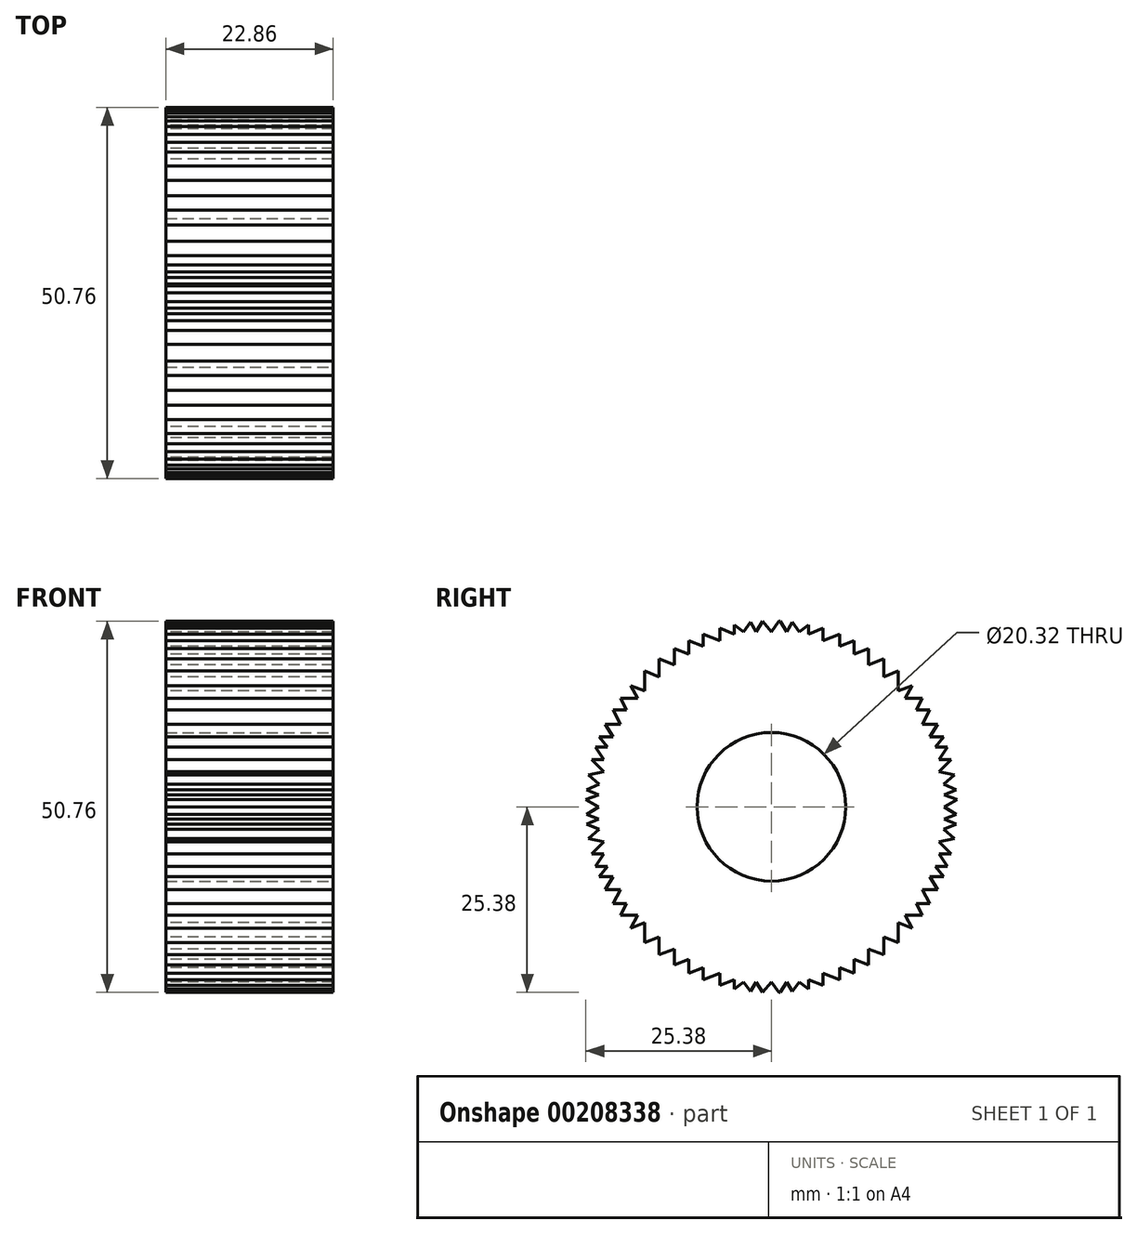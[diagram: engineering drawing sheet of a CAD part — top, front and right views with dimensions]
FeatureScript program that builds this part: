
annotation { "Feature Type Name" : "Feature", "Feature Type Description" : "" }
export const myFeature = defineFeature(function(context is Context, id is Id, definition is map)
    precondition{}
    {
        {
            var Q0;
            Q0=qCreatedBy(makeId("Right.planeOp"),FACE);
            var sketch = newSketch(context, id + "F0", { "sketchPlane" : qUnion([Q0])});
            skCircle(sketch, "E0", {"center": v(0, 0) * mm, "radius": 25.4 * mm});
            skLineSegment(sketch, "E1", {"start": v(-19.24, 16.59) * mm, "end": v(-17.33, 15.84) * mm});
            skLineSegment(sketch, "E2", {"start": v(-17.33, 15.84) * mm, "end": v(-17.33, 18.57) * mm});
            skLineSegment(sketch, "E3", {"start": v(-17.33, 18.57) * mm, "end": v(-15.36, 17.8) * mm});
            skLineSegment(sketch, "E4", {"start": v(-15.36, 17.8) * mm, "end": v(-15.36, 20.23) * mm});
            skLineSegment(sketch, "E5", {"start": v(-15.36, 20.23) * mm, "end": v(-13.3, 19.42) * mm});
            skLineSegment(sketch, "E6", {"start": v(-13.3, 19.42) * mm, "end": v(-13.3, 21.64) * mm});
            skLineSegment(sketch, "E7", {"start": v(-13.3, 21.64) * mm, "end": v(-11.3, 20.86) * mm});
            skLineSegment(sketch, "E8", {"start": v(-11.3, 20.86) * mm, "end": v(-11.3, 22.75) * mm});
            skLineSegment(sketch, "E9", {"start": v(-11.3, 22.75) * mm, "end": v(-9.31, 21.96) * mm});
            skLineSegment(sketch, "E10", {"start": v(-9.31, 21.96) * mm, "end": v(-9.31, 23.63) * mm});
            skLineSegment(sketch, "E11", {"start": v(-9.31, 23.63) * mm, "end": v(-7.06, 22.75) * mm});
            skLineSegment(sketch, "E12", {"start": v(-7.06, 22.75) * mm, "end": v(-7.06, 24.4) * mm});
            skLineSegment(sketch, "E13", {"start": v(-7.06, 24.4) * mm, "end": v(-5.1, 23.63) * mm});
            skLineSegment(sketch, "E14", {"start": v(-5.1, 23.63) * mm, "end": v(-5.1, 24.88) * mm});
            skLineSegment(sketch, "E15", {"start": v(-5.1, 24.88) * mm, "end": v(-3.8, 23.93) * mm});
            skLineSegment(sketch, "E16", {"start": v(-3.8, 23.93) * mm, "end": v(-2.85, 25.24) * mm});
            skLineSegment(sketch, "E17", {"start": v(-2.85, 25.24) * mm, "end": v(-2.1, 23.93) * mm});
            skLineSegment(sketch, "E18", {"start": v(-2.1, 23.93) * mm, "end": v(-1.21, 25.37) * mm});
            skLineSegment(sketch, "E19", {"start": v(-1.21, 25.37) * mm, "end": v(0, 23.93) * mm});
            skLineSegment(sketch, "E20", {"start": v(0, 23.93) * mm, "end": v(1, 25.38) * mm});
            skLineSegment(sketch, "E21", {"start": v(-19.24, 16.59) * mm, "end": v(-18.29, 14.84) * mm});
            skPoint(sketch, "E21.endSnap0", {"position": v(-18.29, 16.21) * mm});
            skLineSegment(sketch, "E22", {"start": v(-18.29, 14.84) * mm, "end": v(-20.62, 14.84) * mm});
            skLineSegment(sketch, "E23", {"start": v(-20.62, 14.84) * mm, "end": v(-19.8, 13.24) * mm});
            skLineSegment(sketch, "E24", {"start": v(-19.8, 13.24) * mm, "end": v(-21.68, 13.24) * mm});
            skLineSegment(sketch, "E25", {"start": v(-21.68, 13.24) * mm, "end": v(-20.62, 11.3) * mm});
            skLineSegment(sketch, "E26", {"start": v(-20.62, 11.3) * mm, "end": v(-22.74, 11.3) * mm});
            skLineSegment(sketch, "E27", {"start": v(-22.74, 11.3) * mm, "end": v(-21.68, 9.54) * mm});
            skLineSegment(sketch, "E28", {"start": v(-21.68, 9.54) * mm, "end": v(-23.54, 9.54) * mm});
            skLineSegment(sketch, "E29", {"start": v(-23.54, 9.54) * mm, "end": v(-22.44, 8.17) * mm});
            skLineSegment(sketch, "E30", {"start": v(-22.44, 8.17) * mm, "end": v(-24.05, 8.17) * mm});
            skLineSegment(sketch, "E31", {"start": v(-24.05, 8.17) * mm, "end": v(-22.93, 6.46) * mm});
            skLineSegment(sketch, "E32", {"start": v(-22.93, 6.46) * mm, "end": v(-24.57, 6.46) * mm});
            skLineSegment(sketch, "E33", {"start": v(-24.57, 6.46) * mm, "end": v(-22.93, 4.8) * mm});
            skLineSegment(sketch, "E34", {"start": v(-22.93, 4.8) * mm, "end": v(-25.03, 4.34) * mm});
            skLineSegment(sketch, "E35", {"start": v(-25.03, 4.34) * mm, "end": v(-23.54, 3.1) * mm});
            skLineSegment(sketch, "E36", {"start": v(-23.54, 3.1) * mm, "end": v(-25.3, 2.36) * mm});
            skLineSegment(sketch, "E37", {"start": v(-25.3, 2.36) * mm, "end": v(-23.65, 1.66) * mm});
            skLineSegment(sketch, "E38", {"start": v(-23.65, 1.66) * mm, "end": v(-25.38, 1.01) * mm});
            skLineSegment(sketch, "E39", {"start": v(-25.38, 1.01) * mm, "end": v(-23.65, 0) * mm});
            skLineSegment(sketch, "E40", {"start": v(-23.65, 0) * mm, "end": v(-25.38, -1.1) * mm});
            skLineSegment(sketch, "E41.MirrorCS", {"start": v(2.1, 23.93) * mm, "end": v(1.21, 25.37) * mm});
            skLineSegment(sketch, "E42.MirrorCS", {"start": v(2.85, 25.24) * mm, "end": v(2.1, 23.93) * mm});
            skLineSegment(sketch, "E43.MirrorCS", {"start": v(3.8, 23.93) * mm, "end": v(2.85, 25.24) * mm});
            skLineSegment(sketch, "E44.MirrorCS", {"start": v(5.1, 24.88) * mm, "end": v(3.8, 23.93) * mm});
            skLineSegment(sketch, "E45.MirrorCS", {"start": v(5.1, 23.63) * mm, "end": v(5.1, 24.88) * mm});
            skLineSegment(sketch, "E46.MirrorCS", {"start": v(7.06, 24.4) * mm, "end": v(5.1, 23.63) * mm});
            skLineSegment(sketch, "E47.MirrorCS", {"start": v(7.06, 22.75) * mm, "end": v(7.06, 24.4) * mm});
            skLineSegment(sketch, "E48.MirrorCS", {"start": v(9.31, 23.63) * mm, "end": v(7.06, 22.75) * mm});
            skLineSegment(sketch, "E49.MirrorCS", {"start": v(9.31, 21.96) * mm, "end": v(9.31, 23.63) * mm});
            skLineSegment(sketch, "E50.MirrorCS", {"start": v(11.3, 22.75) * mm, "end": v(9.31, 21.96) * mm});
            skLineSegment(sketch, "E51.MirrorCS", {"start": v(11.3, 20.86) * mm, "end": v(11.3, 22.75) * mm});
            skLineSegment(sketch, "E52.MirrorCS", {"start": v(13.3, 21.64) * mm, "end": v(11.3, 20.86) * mm});
            skLineSegment(sketch, "E53.MirrorCS", {"start": v(13.3, 19.42) * mm, "end": v(13.3, 21.64) * mm});
            skLineSegment(sketch, "E54.MirrorCS", {"start": v(15.36, 20.23) * mm, "end": v(13.3, 19.42) * mm});
            skLineSegment(sketch, "E55.MirrorCS", {"start": v(15.36, 17.8) * mm, "end": v(15.36, 20.23) * mm});
            skLineSegment(sketch, "E56.MirrorCS", {"start": v(17.33, 18.57) * mm, "end": v(15.36, 17.8) * mm});
            skLineSegment(sketch, "E57.MirrorCS", {"start": v(17.33, 15.84) * mm, "end": v(17.33, 18.57) * mm});
            skLineSegment(sketch, "E58.MirrorCS", {"start": v(19.24, 16.59) * mm, "end": v(17.33, 15.84) * mm});
            skLineSegment(sketch, "E59.MirrorCS", {"start": v(19.24, 16.59) * mm, "end": v(18.29, 14.84) * mm});
            skLineSegment(sketch, "E60.MirrorCS", {"start": v(18.29, 14.84) * mm, "end": v(20.62, 14.84) * mm});
            skLineSegment(sketch, "E61.MirrorCS", {"start": v(20.62, 14.84) * mm, "end": v(19.8, 13.24) * mm});
            skLineSegment(sketch, "E62.MirrorCS", {"start": v(19.8, 13.24) * mm, "end": v(21.68, 13.24) * mm});
            skLineSegment(sketch, "E63.MirrorCS", {"start": v(21.68, 13.24) * mm, "end": v(20.62, 11.3) * mm});
            skLineSegment(sketch, "E64.MirrorCS", {"start": v(20.62, 11.3) * mm, "end": v(22.74, 11.3) * mm});
            skLineSegment(sketch, "E65.MirrorCS", {"start": v(22.74, 11.3) * mm, "end": v(21.68, 9.54) * mm});
            skLineSegment(sketch, "E66.MirrorCS", {"start": v(21.68, 9.54) * mm, "end": v(23.54, 9.54) * mm});
            skLineSegment(sketch, "E67.MirrorCS", {"start": v(23.54, 9.54) * mm, "end": v(22.44, 8.17) * mm});
            skLineSegment(sketch, "E68.MirrorCS", {"start": v(22.44, 8.17) * mm, "end": v(24.05, 8.17) * mm});
            skLineSegment(sketch, "E69.MirrorCS", {"start": v(24.05, 8.17) * mm, "end": v(22.93, 6.46) * mm});
            skLineSegment(sketch, "E70.MirrorCS", {"start": v(22.93, 6.46) * mm, "end": v(24.57, 6.46) * mm});
            skLineSegment(sketch, "E71.MirrorCS", {"start": v(24.57, 6.46) * mm, "end": v(22.93, 4.8) * mm});
            skLineSegment(sketch, "E72.MirrorCS", {"start": v(22.93, 4.8) * mm, "end": v(25.03, 4.34) * mm});
            skLineSegment(sketch, "E73.MirrorCS", {"start": v(25.03, 4.34) * mm, "end": v(23.54, 3.1) * mm});
            skLineSegment(sketch, "E74.MirrorCS", {"start": v(23.54, 3.1) * mm, "end": v(25.3, 2.36) * mm});
            skLineSegment(sketch, "E75.MirrorCS", {"start": v(25.3, 2.36) * mm, "end": v(23.65, 1.66) * mm});
            skLineSegment(sketch, "E76.MirrorCS", {"start": v(23.65, 1.66) * mm, "end": v(25.38, 1.01) * mm});
            skLineSegment(sketch, "E77.MirrorCS", {"start": v(25.38, 1.01) * mm, "end": v(23.65, 0) * mm});
            skLineSegment(sketch, "E78.MirrorCS", {"start": v(23.65, 0) * mm, "end": v(25.38, -1.1) * mm});
            skLineSegment(sketch, "E79.MirrorCS", {"start": v(23.65, -1.66) * mm, "end": v(25.38, -1.01) * mm});
            skLineSegment(sketch, "E80.MirrorCS", {"start": v(25.3, -2.36) * mm, "end": v(23.65, -1.66) * mm});
            skLineSegment(sketch, "E81.MirrorCS", {"start": v(23.54, -3.1) * mm, "end": v(25.3, -2.36) * mm});
            skLineSegment(sketch, "E82.MirrorCS", {"start": v(25.03, -4.34) * mm, "end": v(23.54, -3.1) * mm});
            skLineSegment(sketch, "E83.MirrorCS", {"start": v(22.93, -4.8) * mm, "end": v(25.03, -4.34) * mm});
            skLineSegment(sketch, "E84.MirrorCS", {"start": v(24.57, -6.46) * mm, "end": v(22.93, -4.8) * mm});
            skLineSegment(sketch, "E85.MirrorCS", {"start": v(22.93, -6.46) * mm, "end": v(24.57, -6.46) * mm});
            skLineSegment(sketch, "E86.MirrorCS", {"start": v(24.05, -8.17) * mm, "end": v(22.93, -6.46) * mm});
            skLineSegment(sketch, "E87.MirrorCS", {"start": v(22.44, -8.17) * mm, "end": v(24.05, -8.17) * mm});
            skLineSegment(sketch, "E88.MirrorCS", {"start": v(23.54, -9.54) * mm, "end": v(22.44, -8.17) * mm});
            skLineSegment(sketch, "E89.MirrorCS", {"start": v(21.68, -9.54) * mm, "end": v(23.54, -9.54) * mm});
            skLineSegment(sketch, "E90.MirrorCS", {"start": v(22.74, -11.3) * mm, "end": v(21.68, -9.54) * mm});
            skLineSegment(sketch, "E91.MirrorCS", {"start": v(20.62, -11.3) * mm, "end": v(22.74, -11.3) * mm});
            skLineSegment(sketch, "E92.MirrorCS", {"start": v(21.68, -13.24) * mm, "end": v(20.62, -11.3) * mm});
            skLineSegment(sketch, "E93.MirrorCS", {"start": v(19.8, -13.24) * mm, "end": v(21.68, -13.24) * mm});
            skLineSegment(sketch, "E94.MirrorCS", {"start": v(20.62, -14.84) * mm, "end": v(19.8, -13.24) * mm});
            skLineSegment(sketch, "E95.MirrorCS", {"start": v(18.29, -14.84) * mm, "end": v(20.62, -14.84) * mm});
            skLineSegment(sketch, "E96.MirrorCS", {"start": v(19.24, -16.59) * mm, "end": v(18.29, -14.84) * mm});
            skLineSegment(sketch, "E97.MirrorCS", {"start": v(19.24, -16.59) * mm, "end": v(17.33, -15.84) * mm});
            skLineSegment(sketch, "E98.MirrorCS", {"start": v(17.33, -15.84) * mm, "end": v(17.33, -18.57) * mm});
            skLineSegment(sketch, "E99.MirrorCS", {"start": v(17.33, -18.57) * mm, "end": v(15.36, -17.8) * mm});
            skLineSegment(sketch, "E100.MirrorCS", {"start": v(15.36, -17.8) * mm, "end": v(15.36, -20.23) * mm});
            skLineSegment(sketch, "E101.MirrorCS", {"start": v(15.36, -20.23) * mm, "end": v(13.3, -19.42) * mm});
            skLineSegment(sketch, "E102.MirrorCS", {"start": v(13.3, -19.42) * mm, "end": v(13.3, -21.64) * mm});
            skLineSegment(sketch, "E103.MirrorCS", {"start": v(13.3, -21.64) * mm, "end": v(11.3, -20.86) * mm});
            skLineSegment(sketch, "E104.MirrorCS", {"start": v(-23.65, -1.66) * mm, "end": v(-25.38, -1.01) * mm});
            skLineSegment(sketch, "E105.MirrorCS", {"start": v(-25.3, -2.36) * mm, "end": v(-23.65, -1.66) * mm});
            skLineSegment(sketch, "E106.MirrorCS", {"start": v(-23.54, -3.1) * mm, "end": v(-25.3, -2.36) * mm});
            skLineSegment(sketch, "E107.MirrorCS", {"start": v(-25.03, -4.34) * mm, "end": v(-23.54, -3.1) * mm});
            skLineSegment(sketch, "E108.MirrorCS", {"start": v(-22.93, -4.8) * mm, "end": v(-25.03, -4.34) * mm});
            skLineSegment(sketch, "E109.MirrorCS", {"start": v(-24.57, -6.46) * mm, "end": v(-22.93, -4.8) * mm});
            skLineSegment(sketch, "E110.MirrorCS", {"start": v(-22.93, -6.46) * mm, "end": v(-24.57, -6.46) * mm});
            skLineSegment(sketch, "E111.MirrorCS", {"start": v(-24.05, -8.17) * mm, "end": v(-22.93, -6.46) * mm});
            skLineSegment(sketch, "E112.MirrorCS", {"start": v(-22.44, -8.17) * mm, "end": v(-24.05, -8.17) * mm});
            skLineSegment(sketch, "E113.MirrorCS", {"start": v(-23.54, -9.54) * mm, "end": v(-22.44, -8.17) * mm});
            skLineSegment(sketch, "E114.MirrorCS", {"start": v(-21.68, -9.54) * mm, "end": v(-23.54, -9.54) * mm});
            skLineSegment(sketch, "E115.MirrorCS", {"start": v(-22.74, -11.3) * mm, "end": v(-21.68, -9.54) * mm});
            skLineSegment(sketch, "E116.MirrorCS", {"start": v(-20.62, -11.3) * mm, "end": v(-22.74, -11.3) * mm});
            skLineSegment(sketch, "E117.MirrorCS", {"start": v(-21.68, -13.24) * mm, "end": v(-20.62, -11.3) * mm});
            skLineSegment(sketch, "E118.MirrorCS", {"start": v(-19.8, -13.24) * mm, "end": v(-21.68, -13.24) * mm});
            skLineSegment(sketch, "E119.MirrorCS", {"start": v(-20.62, -14.84) * mm, "end": v(-19.8, -13.24) * mm});
            skLineSegment(sketch, "E120.MirrorCS", {"start": v(-18.29, -14.84) * mm, "end": v(-20.62, -14.84) * mm});
            skLineSegment(sketch, "E121.MirrorCS", {"start": v(-19.24, -16.59) * mm, "end": v(-18.29, -14.84) * mm});
            skLineSegment(sketch, "E122.MirrorCS", {"start": v(-17.33, -15.84) * mm, "end": v(-17.33, -18.57) * mm});
            skPoint(sketch, "E123.MirrorP", {"position": v(-18.29, -16.21) * mm});
            skLineSegment(sketch, "E124.MirrorCS", {"start": v(-19.24, -16.59) * mm, "end": v(-17.33, -15.84) * mm});
            skLineSegment(sketch, "E125.MirrorCS", {"start": v(-17.33, -18.57) * mm, "end": v(-15.36, -17.8) * mm});
            skLineSegment(sketch, "E126.MirrorCS", {"start": v(-15.36, -17.8) * mm, "end": v(-15.36, -20.23) * mm});
            skLineSegment(sketch, "E127.MirrorCS", {"start": v(-15.36, -20.23) * mm, "end": v(-13.3, -19.42) * mm});
            skLineSegment(sketch, "E128.MirrorCS", {"start": v(-13.3, -19.42) * mm, "end": v(-13.3, -21.64) * mm});
            skLineSegment(sketch, "E129.MirrorCS", {"start": v(-13.3, -21.64) * mm, "end": v(-11.3, -20.86) * mm});
            skLineSegment(sketch, "E130.MirrorCS", {"start": v(-11.3, -20.86) * mm, "end": v(-11.3, -22.75) * mm});
            skLineSegment(sketch, "E131.MirrorCS", {"start": v(-11.3, -22.75) * mm, "end": v(-9.31, -21.96) * mm});
            skLineSegment(sketch, "E132.MirrorCS", {"start": v(-9.31, -21.96) * mm, "end": v(-9.31, -23.63) * mm});
            skLineSegment(sketch, "E133.MirrorCS", {"start": v(-9.31, -23.63) * mm, "end": v(-7.06, -22.75) * mm});
            skLineSegment(sketch, "E134.MirrorCS", {"start": v(-7.06, -22.75) * mm, "end": v(-7.06, -24.4) * mm});
            skLineSegment(sketch, "E135.MirrorCS", {"start": v(-7.06, -24.4) * mm, "end": v(-5.1, -23.63) * mm});
            skLineSegment(sketch, "E136.MirrorCS", {"start": v(-5.1, -23.63) * mm, "end": v(-5.1, -24.88) * mm});
            skLineSegment(sketch, "E137.MirrorCS", {"start": v(-5.1, -24.88) * mm, "end": v(-3.8, -23.93) * mm});
            skLineSegment(sketch, "E138.MirrorCS", {"start": v(-3.8, -23.93) * mm, "end": v(-2.85, -25.24) * mm});
            skLineSegment(sketch, "E139.MirrorCS", {"start": v(-2.85, -25.24) * mm, "end": v(-2.1, -23.93) * mm});
            skLineSegment(sketch, "E140.MirrorCS", {"start": v(-2.1, -23.93) * mm, "end": v(-1.21, -25.37) * mm});
            skLineSegment(sketch, "E141.MirrorCS", {"start": v(-1.21, -25.37) * mm, "end": v(0, -23.93) * mm});
            skLineSegment(sketch, "E142.MirrorCS", {"start": v(0, -23.93) * mm, "end": v(1, -25.38) * mm});
            skLineSegment(sketch, "E143.MirrorCS", {"start": v(2.1, -23.93) * mm, "end": v(1.21, -25.37) * mm});
            skLineSegment(sketch, "E144.MirrorCS", {"start": v(9.31, -23.63) * mm, "end": v(7.06, -22.75) * mm});
            skLineSegment(sketch, "E145.MirrorCS", {"start": v(9.31, -21.96) * mm, "end": v(9.31, -23.63) * mm});
            skLineSegment(sketch, "E146.MirrorCS", {"start": v(11.3, -22.75) * mm, "end": v(9.31, -21.96) * mm});
            skLineSegment(sketch, "E147.MirrorCS", {"start": v(11.3, -20.86) * mm, "end": v(11.3, -22.75) * mm});
            skLineSegment(sketch, "E148.MirrorCS", {"start": v(7.06, -24.4) * mm, "end": v(5.1, -23.63) * mm});
            skLineSegment(sketch, "E149.MirrorCS", {"start": v(7.06, -22.75) * mm, "end": v(7.06, -24.4) * mm});
            skLineSegment(sketch, "E150.MirrorCS", {"start": v(2.85, -25.24) * mm, "end": v(2.1, -23.93) * mm});
            skLineSegment(sketch, "E151.MirrorCS", {"start": v(5.1, -24.88) * mm, "end": v(3.8, -23.93) * mm});
            skLineSegment(sketch, "E152.MirrorCS", {"start": v(5.1, -23.63) * mm, "end": v(5.1, -24.88) * mm});
            skLineSegment(sketch, "E153.MirrorCS", {"start": v(3.8, -23.93) * mm, "end": v(2.85, -25.24) * mm});
            skSolve(sketch);
        }
        {
            var Q0;
            Q0=makeQuery(id+"F0.imprint","IMPRINT",FACE,{"disambiguationData":[TD([[makeQuery(id+"F0.imprint","IMPRINT",EDGE,{"derivedFrom":sQuery(id+"F0.wireOp",EDGE,"E1")}),-1.0]])]});
            extrude(context, id + "F1", {"entities" : qUnion([Q0]), "depth" : 22.86 * mm});
        }
        {
            var Q0;
            Q0=makeQuery(id+"F1.opExtrude","CAP_FACE",FACE,{"disambiguationData":[OSD([sQuery(id+"F0.wireOp",EDGE,"E0"),sQuery(id+"F0.wireOp",EDGE,"E1"),sQuery(id+"F0.wireOp",EDGE,"E2"),sQuery(id+"F0.wireOp",EDGE,"E3"),sQuery(id+"F0.wireOp",EDGE,"E4"),sQuery(id+"F0.wireOp",EDGE,"E5"),sQuery(id+"F0.wireOp",EDGE,"E6"),sQuery(id+"F0.wireOp",EDGE,"E7"),sQuery(id+"F0.wireOp",EDGE,"E8"),sQuery(id+"F0.wireOp",EDGE,"E9"),sQuery(id+"F0.wireOp",EDGE,"E10"),sQuery(id+"F0.wireOp",EDGE,"E11"),sQuery(id+"F0.wireOp",EDGE,"E12"),sQuery(id+"F0.wireOp",EDGE,"E13"),sQuery(id+"F0.wireOp",EDGE,"E14"),sQuery(id+"F0.wireOp",EDGE,"E15"),sQuery(id+"F0.wireOp",EDGE,"E16"),sQuery(id+"F0.wireOp",EDGE,"E17"),sQuery(id+"F0.wireOp",EDGE,"E18"),sQuery(id+"F0.wireOp",EDGE,"E19"),sQuery(id+"F0.wireOp",EDGE,"E20"),sQuery(id+"F0.wireOp",EDGE,"E21"),sQuery(id+"F0.wireOp",EDGE,"E22"),sQuery(id+"F0.wireOp",EDGE,"E23"),sQuery(id+"F0.wireOp",EDGE,"E24"),sQuery(id+"F0.wireOp",EDGE,"E25"),sQuery(id+"F0.wireOp",EDGE,"E26"),sQuery(id+"F0.wireOp",EDGE,"E27"),sQuery(id+"F0.wireOp",EDGE,"E28"),sQuery(id+"F0.wireOp",EDGE,"E29"),sQuery(id+"F0.wireOp",EDGE,"E30"),sQuery(id+"F0.wireOp",EDGE,"E31"),sQuery(id+"F0.wireOp",EDGE,"E32"),sQuery(id+"F0.wireOp",EDGE,"E33"),sQuery(id+"F0.wireOp",EDGE,"E34"),sQuery(id+"F0.wireOp",EDGE,"E35"),sQuery(id+"F0.wireOp",EDGE,"E36"),sQuery(id+"F0.wireOp",EDGE,"E37"),sQuery(id+"F0.wireOp",EDGE,"E38"),sQuery(id+"F0.wireOp",EDGE,"E39"),sQuery(id+"F0.wireOp",EDGE,"E40"),sQuery(id+"F0.wireOp",EDGE,"E41.MirrorCS"),sQuery(id+"F0.wireOp",EDGE,"E42.MirrorCS"),sQuery(id+"F0.wireOp",EDGE,"E43.MirrorCS"),sQuery(id+"F0.wireOp",EDGE,"E44.MirrorCS"),sQuery(id+"F0.wireOp",EDGE,"E45.MirrorCS"),sQuery(id+"F0.wireOp",EDGE,"E46.MirrorCS"),sQuery(id+"F0.wireOp",EDGE,"E47.MirrorCS"),sQuery(id+"F0.wireOp",EDGE,"E48.MirrorCS"),sQuery(id+"F0.wireOp",EDGE,"E49.MirrorCS"),sQuery(id+"F0.wireOp",EDGE,"E50.MirrorCS"),sQuery(id+"F0.wireOp",EDGE,"E51.MirrorCS"),sQuery(id+"F0.wireOp",EDGE,"E52.MirrorCS"),sQuery(id+"F0.wireOp",EDGE,"E53.MirrorCS"),sQuery(id+"F0.wireOp",EDGE,"E54.MirrorCS"),sQuery(id+"F0.wireOp",EDGE,"E55.MirrorCS"),sQuery(id+"F0.wireOp",EDGE,"E56.MirrorCS"),sQuery(id+"F0.wireOp",EDGE,"E57.MirrorCS"),sQuery(id+"F0.wireOp",EDGE,"E58.MirrorCS"),sQuery(id+"F0.wireOp",EDGE,"E59.MirrorCS"),sQuery(id+"F0.wireOp",EDGE,"E60.MirrorCS"),sQuery(id+"F0.wireOp",EDGE,"E61.MirrorCS"),sQuery(id+"F0.wireOp",EDGE,"E62.MirrorCS"),sQuery(id+"F0.wireOp",EDGE,"E63.MirrorCS"),sQuery(id+"F0.wireOp",EDGE,"E64.MirrorCS"),sQuery(id+"F0.wireOp",EDGE,"E65.MirrorCS"),sQuery(id+"F0.wireOp",EDGE,"E66.MirrorCS"),sQuery(id+"F0.wireOp",EDGE,"E67.MirrorCS"),sQuery(id+"F0.wireOp",EDGE,"E68.MirrorCS"),sQuery(id+"F0.wireOp",EDGE,"E69.MirrorCS"),sQuery(id+"F0.wireOp",EDGE,"E70.MirrorCS"),sQuery(id+"F0.wireOp",EDGE,"E71.MirrorCS"),sQuery(id+"F0.wireOp",EDGE,"E72.MirrorCS"),sQuery(id+"F0.wireOp",EDGE,"E73.MirrorCS"),sQuery(id+"F0.wireOp",EDGE,"E74.MirrorCS"),sQuery(id+"F0.wireOp",EDGE,"E75.MirrorCS"),sQuery(id+"F0.wireOp",EDGE,"E76.MirrorCS"),sQuery(id+"F0.wireOp",EDGE,"E77.MirrorCS"),sQuery(id+"F0.wireOp",EDGE,"E78.MirrorCS"),sQuery(id+"F0.wireOp",EDGE,"E79.MirrorCS"),sQuery(id+"F0.wireOp",EDGE,"E80.MirrorCS"),sQuery(id+"F0.wireOp",EDGE,"E81.MirrorCS"),sQuery(id+"F0.wireOp",EDGE,"E82.MirrorCS"),sQuery(id+"F0.wireOp",EDGE,"E83.MirrorCS"),sQuery(id+"F0.wireOp",EDGE,"E84.MirrorCS"),sQuery(id+"F0.wireOp",EDGE,"E85.MirrorCS"),sQuery(id+"F0.wireOp",EDGE,"E86.MirrorCS"),sQuery(id+"F0.wireOp",EDGE,"E87.MirrorCS"),sQuery(id+"F0.wireOp",EDGE,"E88.MirrorCS"),sQuery(id+"F0.wireOp",EDGE,"E89.MirrorCS"),sQuery(id+"F0.wireOp",EDGE,"E90.MirrorCS"),sQuery(id+"F0.wireOp",EDGE,"E91.MirrorCS"),sQuery(id+"F0.wireOp",EDGE,"E92.MirrorCS"),sQuery(id+"F0.wireOp",EDGE,"E93.MirrorCS"),sQuery(id+"F0.wireOp",EDGE,"E94.MirrorCS"),sQuery(id+"F0.wireOp",EDGE,"E95.MirrorCS"),sQuery(id+"F0.wireOp",EDGE,"E96.MirrorCS"),sQuery(id+"F0.wireOp",EDGE,"E97.MirrorCS"),sQuery(id+"F0.wireOp",EDGE,"E98.MirrorCS"),sQuery(id+"F0.wireOp",EDGE,"E99.MirrorCS"),sQuery(id+"F0.wireOp",EDGE,"E104.MirrorCS"),sQuery(id+"F0.wireOp",EDGE,"E105.MirrorCS"),sQuery(id+"F0.wireOp",EDGE,"E106.MirrorCS"),sQuery(id+"F0.wireOp",EDGE,"E107.MirrorCS"),sQuery(id+"F0.wireOp",EDGE,"E108.MirrorCS"),sQuery(id+"F0.wireOp",EDGE,"E109.MirrorCS"),sQuery(id+"F0.wireOp",EDGE,"E110.MirrorCS"),sQuery(id+"F0.wireOp",EDGE,"E111.MirrorCS"),sQuery(id+"F0.wireOp",EDGE,"E112.MirrorCS"),sQuery(id+"F0.wireOp",EDGE,"E113.MirrorCS"),sQuery(id+"F0.wireOp",EDGE,"E114.MirrorCS"),sQuery(id+"F0.wireOp",EDGE,"E115.MirrorCS"),sQuery(id+"F0.wireOp",EDGE,"E116.MirrorCS"),sQuery(id+"F0.wireOp",EDGE,"E119.MirrorCS"),sQuery(id+"F0.wireOp",EDGE,"E118.MirrorCS"),sQuery(id+"F0.wireOp",EDGE,"E117.MirrorCS"),sQuery(id+"F0.wireOp",EDGE,"E120.MirrorCS"),sQuery(id+"F0.wireOp",EDGE,"E121.MirrorCS"),sQuery(id+"F0.wireOp",EDGE,"E124.MirrorCS"),sQuery(id+"F0.wireOp",EDGE,"E122.MirrorCS"),sQuery(id+"F0.wireOp",EDGE,"E125.MirrorCS"),sQuery(id+"F0.wireOp",EDGE,"E126.MirrorCS"),sQuery(id+"F0.wireOp",EDGE,"E127.MirrorCS"),sQuery(id+"F0.wireOp",EDGE,"E128.MirrorCS"),sQuery(id+"F0.wireOp",EDGE,"E129.MirrorCS"),sQuery(id+"F0.wireOp",EDGE,"E130.MirrorCS"),sQuery(id+"F0.wireOp",EDGE,"E146.MirrorCS"),sQuery(id+"F0.wireOp",EDGE,"E147.MirrorCS"),sQuery(id+"F0.wireOp",EDGE,"E103.MirrorCS"),sQuery(id+"F0.wireOp",EDGE,"E102.MirrorCS"),sQuery(id+"F0.wireOp",EDGE,"E101.MirrorCS"),sQuery(id+"F0.wireOp",EDGE,"E100.MirrorCS"),sQuery(id+"F0.wireOp",EDGE,"E148.MirrorCS"),sQuery(id+"F0.wireOp",EDGE,"E149.MirrorCS"),sQuery(id+"F0.wireOp",EDGE,"E144.MirrorCS"),sQuery(id+"F0.wireOp",EDGE,"E145.MirrorCS"),sQuery(id+"F0.wireOp",EDGE,"E143.MirrorCS"),sQuery(id+"F0.wireOp",EDGE,"E152.MirrorCS"),sQuery(id+"F0.wireOp",EDGE,"E140.MirrorCS"),sQuery(id+"F0.wireOp",EDGE,"E141.MirrorCS"),sQuery(id+"F0.wireOp",EDGE,"E142.MirrorCS"),sQuery(id+"F0.wireOp",EDGE,"E131.MirrorCS"),sQuery(id+"F0.wireOp",EDGE,"E132.MirrorCS"),sQuery(id+"F0.wireOp",EDGE,"E133.MirrorCS"),sQuery(id+"F0.wireOp",EDGE,"E134.MirrorCS"),sQuery(id+"F0.wireOp",EDGE,"E135.MirrorCS"),sQuery(id+"F0.wireOp",EDGE,"E136.MirrorCS"),sQuery(id+"F0.wireOp",EDGE,"E137.MirrorCS"),sQuery(id+"F0.wireOp",EDGE,"E138.MirrorCS"),sQuery(id+"F0.wireOp",EDGE,"E139.MirrorCS"),sQuery(id+"F0.wireOp",EDGE,"E150.MirrorCS"),sQuery(id+"F0.wireOp",EDGE,"E151.MirrorCS"),sQuery(id+"F0.wireOp",EDGE,"E153.MirrorCS")])],"isStart":false});
            var sketch = newSketch(context, id + "F2", { "sketchPlane" : qUnion([Q0])});
            skCircle(sketch, "E154", {"center": v(0, 0) * mm, "radius": 10.16 * mm});
            skSolve(sketch);
        }
        {
            var Q0;
            Q0=makeQuery(id+"F2.imprint","IMPRINT",FACE,{"disambiguationData":[TD([[makeQuery(id+"F2.imprint","IMPRINT",EDGE,{"derivedFrom":sQuery(id+"F2.wireOp",EDGE,"E154")}),1.0]])]});
            var Q1;
            Q1=sQuery(id+"F2.wireOp",EDGE,"E154");
            extrude(context, id + "F3", {"entities" : qUnion([Q0]), "operationType" : NewBodyOperationType.REMOVE, "surfaceEntities" : qUnion([Q1]), "oppositeDirection" : true, "depth" : 38.1 * mm});
        }
    });
